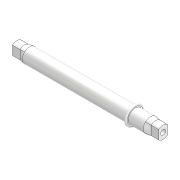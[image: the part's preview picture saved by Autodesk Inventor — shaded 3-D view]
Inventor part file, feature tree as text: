
AUTODESK INVENTOR PART (.ipt)
format: ipt  version: 2022 (Build 260153000, 153)  size: 171,008 bytes
history: native  units: mm
features: sketch x4, extrude x3, plane x2, other x2, loft x1, fillet x1, hole x1, mirror x1, projected_geometry x1
ambient origin geometry x8: Origin, YZ Plane, XZ Plane, XY Plane, X Axis, Y Axis, Z Axis, Center Point
bodies: Solid1 (feature_tree)
feature tree (16):
  extrude  "Shaft"  Depth=3.0mm TaperAngle=0.0deg
  plane  "Work Plane1"
  extrude  "Wheel Insert Profile"  [1 undecoded]
  loft  "Loft1"
  plane  "Work Plane2"
  extrude  "Stopper"  Depth=3.5mm
  fillet  "Fillet1"  [1 undecoded]
  hole  "Hole1"  [1 undecoded]
  mirror  "Mirror1"
  sketch  "Sketch1"  dims[d2=0.0mm d25=3.0mm d26=0.0mm]
  sketch  "Sketch3"  dims[d29=2.0mm d32=0.0mm d33=90.0deg d34=-43.0mm]
  sketch  "Sketch4"  dims[d35=7.5mm d36=1.0mm d37=0.0mm]
  projected_geometry  "Projected Loop1"
  other  "Edges2"
  other  "Edges5"
  sketch  "Sketch9"  dims[d38=0.5mm d76=3.5mm d77=5.0mm d78=0.0mm d79=90.0deg d82=2.0mm d83=6.0mm d84=4.0mm d85=2.0mm d86=90.0deg d87=7.0mm d88=0.0mm]
note: 3 required parameter values undecoded (feature->parameter linkage not recoverable at this tier; creation-order binding heuristic only, values carry confidence <= 0.55)
